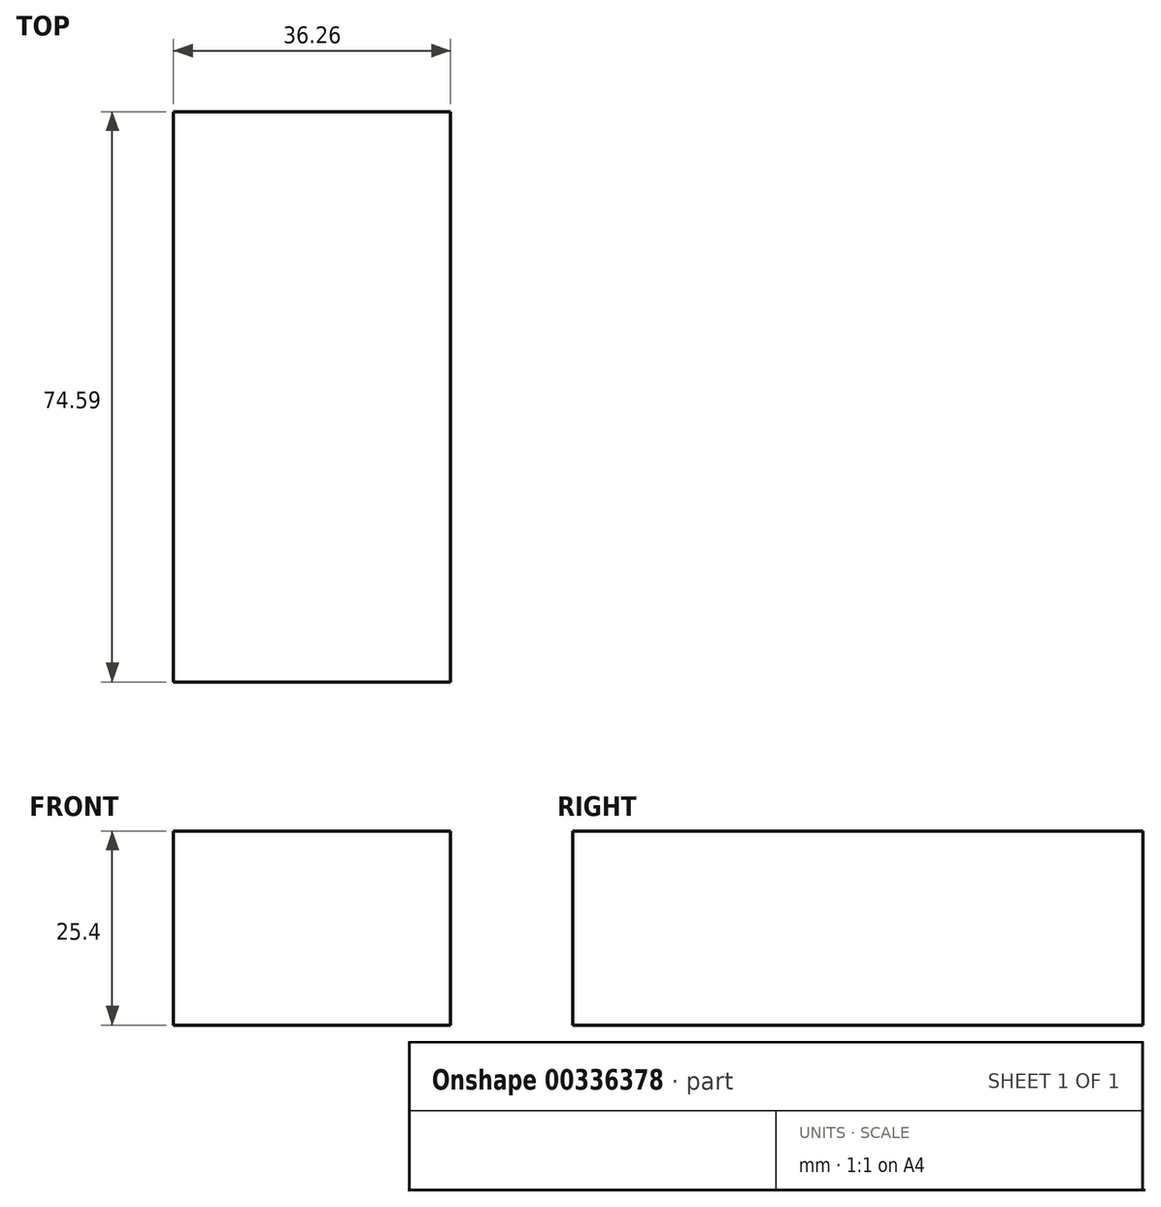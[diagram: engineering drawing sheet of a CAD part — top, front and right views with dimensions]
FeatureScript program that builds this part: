
annotation { "Feature Type Name" : "Feature", "Feature Type Description" : "" }
export const myFeature = defineFeature(function(context is Context, id is Id, definition is map)
    precondition{}
    {
        {
            var Q0;
            Q0=qCreatedBy(makeId("Top.planeOp"),FACE);
            var sketch = newSketch(context, id + "F0", { "sketchPlane" : qUnion([Q0])});
            skLineSegment(sketch, "E0.bottom", {"start": v(-36.26, 74.59) * mm, "end": v(0, 74.59) * mm});
            skLineSegment(sketch, "E0.top", {"start": v(-36.26, 0) * mm, "end": v(0, 0) * mm});
            skLineSegment(sketch, "E0.left", {"start": v(0, 0) * mm, "end": v(0, 74.59) * mm});
            skLineSegment(sketch, "E0.right", {"start": v(-36.26, 0) * mm, "end": v(-36.26, 74.59) * mm});
            skSolve(sketch);
        }
        {
            var Q0;
            Q0=makeQuery(id+"F0.imprint","IMPRINT",FACE,{"disambiguationData":[TD([[makeQuery(id+"F0.imprint","IMPRINT",EDGE,{"derivedFrom":sQuery(id+"F0.wireOp",EDGE,"E0.bottom")}),-1.0]])]});
            extrude(context, id + "F1", {"entities" : qUnion([Q0]), "depth" : 25.4 * mm});
        }
    });
